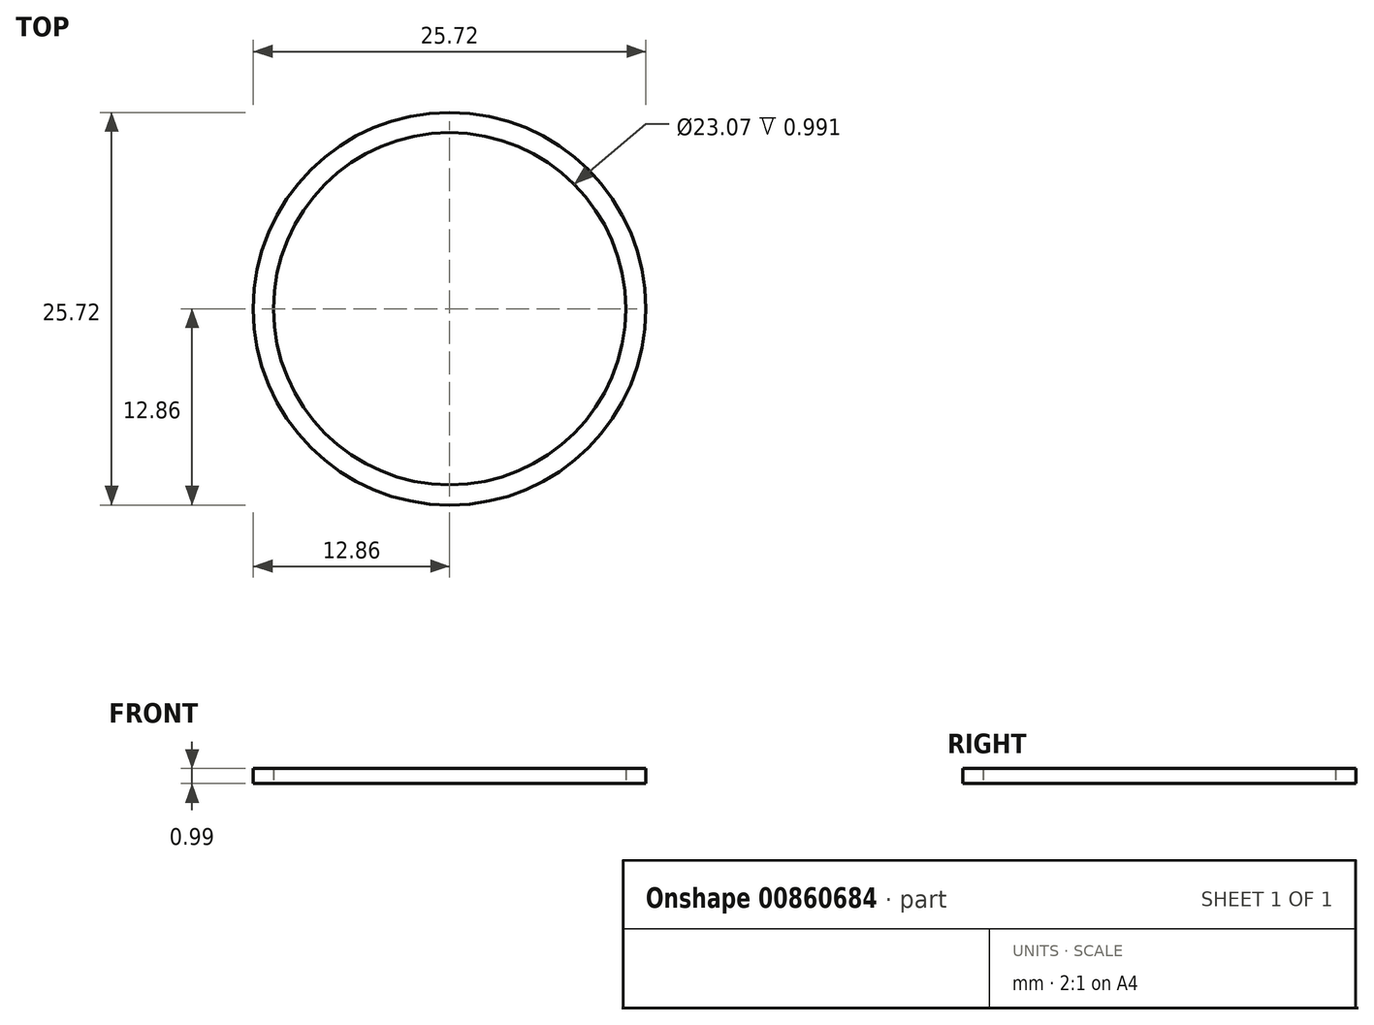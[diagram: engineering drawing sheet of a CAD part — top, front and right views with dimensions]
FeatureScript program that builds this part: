
annotation { "Feature Type Name" : "Feature", "Feature Type Description" : "" }
export const myFeature = defineFeature(function(context is Context, id is Id, definition is map)
    precondition{}
    {
        {
            var Q0;
            Q0=qCreatedBy(makeId("Top.planeOp"),FACE);
            var sketch = newSketch(context, id + "F0", { "sketchPlane" : qUnion([Q0])});
            skCircle(sketch, "E0", {"center": v(0, 0) * mm, "radius": 12.86 * mm});
            skCircle(sketch, "E1", {"center": v(0, 0) * mm, "radius": 11.53 * mm});
            skSolve(sketch);
        }
        {
            var Q0;
            Q0 = qSketchRegion(id + "F0", true);
            extrude(context, id + "F1", {"entities" : qUnion([Q0]), "depth" : 1 * mm, "offsetDistance" : 25.4 * mm});
        }
    });
